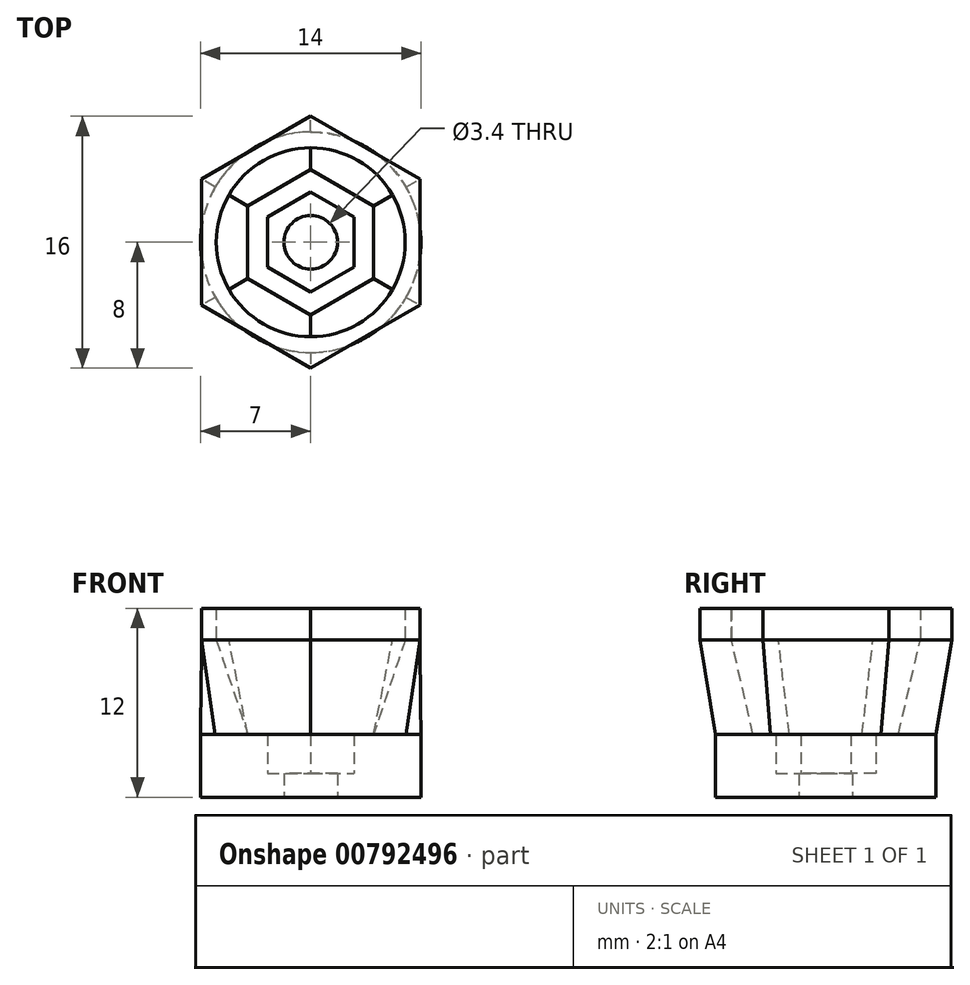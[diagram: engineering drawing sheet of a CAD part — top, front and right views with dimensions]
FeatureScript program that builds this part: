
annotation { "Feature Type Name" : "Feature", "Feature Type Description" : "" }
export const myFeature = defineFeature(function(context is Context, id is Id, definition is map)
    precondition{}
    {
        {
            var Q0;
            Q0=qCreatedBy(makeId("Top.planeOp"),FACE);
            var sketch = newSketch(context, id + "F0", { "sketchPlane" : qUnion([Q0])});
            skCircle(sketch, "E0", {"center": v(0, 0) * mm, "radius": 1.7 * mm});
            skCircle(sketch, "E1.cCircle", {"center": v(0, 0) * mm, "radius": 2.75 * mm, "construction": true});
            skLineSegment(sketch, "E1.0", {"start": v(2.75, 1.59) * mm, "end": v(2.75, -1.59) * mm});
            skLineSegment(sketch, "E1.1", {"start": v(2.75, -1.59) * mm, "end": v(0, -3.18) * mm});
            skLineSegment(sketch, "E1.2", {"start": v(0, -3.18) * mm, "end": v(-2.75, -1.59) * mm});
            skLineSegment(sketch, "E1.3", {"start": v(-2.75, -1.59) * mm, "end": v(-2.75, 1.59) * mm});
            skLineSegment(sketch, "E1.4", {"start": v(-2.75, 1.59) * mm, "end": v(0, 3.18) * mm});
            skLineSegment(sketch, "E1.5", {"start": v(0, 3.18) * mm, "end": v(2.75, 1.59) * mm});
            skPoint(sketch, "E1.0.midPoint", {"position": v(2.75, 0) * mm});
            skCircle(sketch, "E2", {"center": v(0, 0) * mm, "radius": 7 * mm});
            skSolve(sketch);
        }
        {
            var Q0;
            Q0=makeQuery(id+"F0.imprint","IMPRINT",FACE,{"disambiguationData":[TD([[makeQuery(id+"F0.imprint","IMPRINT",EDGE,{"derivedFrom":sQuery(id+"F0.wireOp",EDGE,"E1.0")}),1.0]])]});
            var Q1;
            Q1=makeQuery(id+"F0.imprint","IMPRINT",FACE,{"disambiguationData":[TD([[makeQuery(id+"F0.imprint","IMPRINT",EDGE,{"derivedFrom":sQuery(id+"F0.wireOp",EDGE,"E0")}),-1.0]])]});
            extrude(context, id + "F1", {"entities" : qUnion([Q0, Q1]), "depth" : 4 * mm, "offsetDistance" : 25 * mm});
        }
        {
            var Q0;
            Q0=makeQuery(id+"F0.imprint","IMPRINT",FACE,{"disambiguationData":[TD([[makeQuery(id+"F0.imprint","IMPRINT",EDGE,{"derivedFrom":sQuery(id+"F0.wireOp",EDGE,"E0")}),-1.0]])]});
            extrude(context, id + "F2", {"entities" : qUnion([Q0]), "operationType" : NewBodyOperationType.REMOVE, "depth" : 25 * mm, "offsetDistance" : 25 * mm, "hasSecondDirection" : true, "secondDirectionOppositeDirection" : false, "secondDirectionDepth" : 1.5 * mm});
        }
        {
            var Q0;
            Q0=qCreatedBy(makeId("Top.planeOp"),FACE);
            cPlane(context, id + "F3", {"entities" : qUnion([Q0]), "cplaneType" : CPlaneType.OFFSET, "offset" : 10 * mm, "width" : 150 * mm, "height" : 150 * mm});
        }
        {
            var Q0;
            Q0=makeQuery(id+"F1.opExtrude","CAP_FACE",FACE,{"disambiguationData":[OSD([sQuery(id+"F0.wireOp",EDGE,"E0"),sQuery(id+"F0.wireOp",EDGE,"E2")])],"isStart":false});
            cPlane(context, id + "F4", {"entities" : qUnion([Q0]), "cplaneType" : CPlaneType.OFFSET, "offset" : 0 * mm, "width" : 150 * mm, "height" : 150 * mm});
        }
        {
            var Q0;
            Q0=qCreatedBy(id+"F4.planeOp",FACE);
            var sketch = newSketch(context, id + "F5", { "sketchPlane" : qUnion([Q0])});
            skCircle(sketch, "E3", {"center": v(0, 0) * mm, "radius": 7 * mm});
            skSolve(sketch);
        }
        {
            var Q0;
            Q0=qCreatedBy(id+"F3.planeOp",FACE);
            var sketch = newSketch(context, id + "F6", { "sketchPlane" : qUnion([Q0])});
            skCircle(sketch, "E4.cCircle", {"center": v(0, 0) * mm, "radius": 6.93 * mm, "construction": true});
            skLineSegment(sketch, "E4.0", {"start": v(6.93, 4) * mm, "end": v(6.93, -4) * mm});
            skLineSegment(sketch, "E4.1", {"start": v(6.93, -4) * mm, "end": v(0, -8) * mm});
            skLineSegment(sketch, "E4.2", {"start": v(0, -8) * mm, "end": v(-6.93, -4) * mm});
            skLineSegment(sketch, "E4.3", {"start": v(-6.93, -4) * mm, "end": v(-6.93, 4) * mm});
            skLineSegment(sketch, "E4.4", {"start": v(-6.93, 4) * mm, "end": v(0, 8) * mm});
            skLineSegment(sketch, "E4.5", {"start": v(0, 8) * mm, "end": v(6.93, 4) * mm});
            skPoint(sketch, "E4.0.midPoint", {"position": v(6.93, 0) * mm});
            skSolve(sketch);
        }
        {
            var Q1;
            Q1=qSketchRegion(id+"F5",true);
            var Q2;
            Q2=qSketchRegion(id+"F6",true);
            loft(context, id + "F7", {"operationType" : NewBodyOperationType.ADD, "sheetProfilesArray" : [{ "sheetProfileEntities" : qUnion([Q1]) }, { "sheetProfileEntities" : qUnion([Q2]) }]});
        }
        {
            var Q0;
            Q0=qCreatedBy(id+"F4.planeOp",FACE);
            var sketch = newSketch(context, id + "F8", { "sketchPlane" : qUnion([Q0])});
            skCircle(sketch, "E5.cCircle", {"center": v(0, 0) * mm, "radius": 4 * mm, "construction": true});
            skLineSegment(sketch, "E5.0", {"start": v(4, 2.3) * mm, "end": v(4, -2.3) * mm});
            skLineSegment(sketch, "E5.1", {"start": v(4, -2.3) * mm, "end": v(0, -4.62) * mm});
            skLineSegment(sketch, "E5.2", {"start": v(0, -4.62) * mm, "end": v(-4, -2.3) * mm});
            skLineSegment(sketch, "E5.3", {"start": v(-4, -2.3) * mm, "end": v(-4, 2.3) * mm});
            skLineSegment(sketch, "E5.4", {"start": v(-4, 2.3) * mm, "end": v(0, 4.62) * mm});
            skLineSegment(sketch, "E5.5", {"start": v(0, 4.62) * mm, "end": v(4, 2.3) * mm});
            skPoint(sketch, "E5.0.midPoint", {"position": v(4, 0) * mm});
            skSolve(sketch);
        }
        {
            var Q0;
            Q0=qCreatedBy(id+"F3.planeOp",FACE);
            var sketch = newSketch(context, id + "F9", { "sketchPlane" : qUnion([Q0])});
            skCircle(sketch, "E6", {"center": v(0, 0) * mm, "radius": 6 * mm});
            skSolve(sketch);
        }
        {
            var Q1;
            Q1=qSketchRegion(id+"F8",true);
            var Q2;
            Q2=qSketchRegion(id+"F9",true);
            loft(context, id + "F10", {"operationType" : NewBodyOperationType.REMOVE, "sheetProfilesArray" : [{ "sheetProfileEntities" : qUnion([Q1]) }, { "sheetProfileEntities" : qUnion([Q2]) }]});
        }
        {
            var Q0;
            Q0=makeQuery(id+"F7.opLoft","CAP_FACE",FACE,{"disambiguationData":[OSD([makeQuery(id+"F6.imprint","IMPRINT",FACE,{"disambiguationData":[TD([[makeQuery(id+"F6.imprint","IMPRINT",EDGE,{"derivedFrom":sQuery(id+"F6.wireOp",EDGE,"E4.0")}),-1.0]])]})])],"isStart":true});
            extrude(context, id + "F11", {"entities" : qUnion([Q0]), "operationType" : NewBodyOperationType.ADD, "depth" : 2 * mm, "offsetDistance" : 25 * mm});
        }
    });
